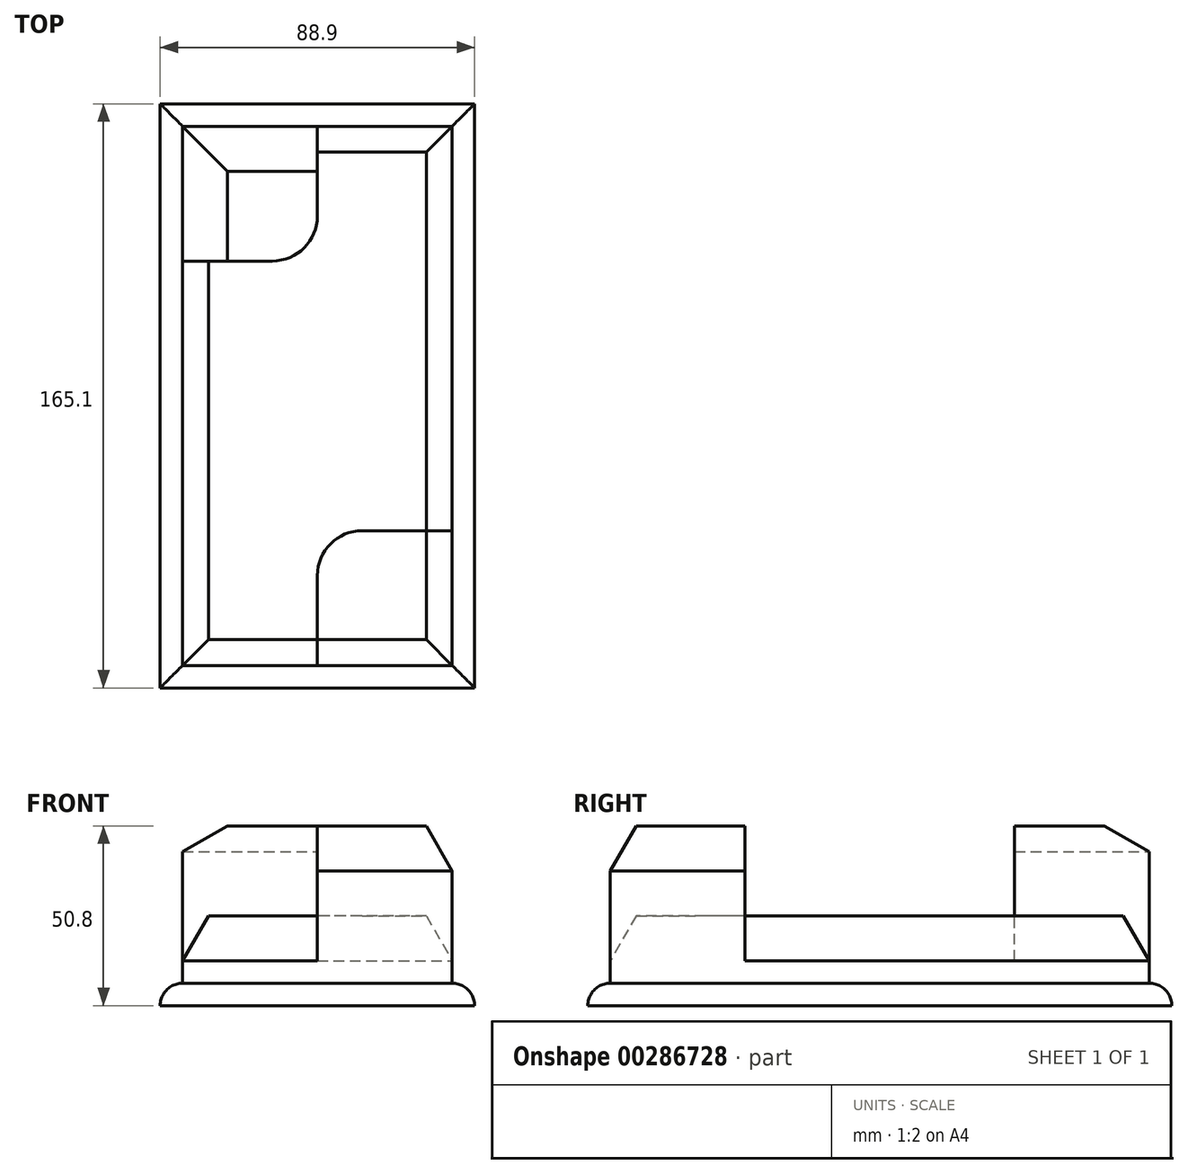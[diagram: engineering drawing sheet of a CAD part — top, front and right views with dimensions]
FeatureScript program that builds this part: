
annotation { "Feature Type Name" : "Feature", "Feature Type Description" : "" }
export const myFeature = defineFeature(function(context is Context, id is Id, definition is map)
    precondition{}
    {
        {
            var Q0;
            Q0=qCreatedBy(makeId("Top.planeOp"),FACE);
            var sketch = newSketch(context, id + "F0", { "sketchPlane" : qUnion([Q0])});
            skLineSegment(sketch, "E0.bottom", {"start": v(0, 0) * mm, "end": v(76.2, 0) * mm});
            skLineSegment(sketch, "E0.top", {"start": v(0, -152.4) * mm, "end": v(76.2, -152.4) * mm});
            skLineSegment(sketch, "E0.left", {"start": v(0, 0) * mm, "end": v(0, -152.4) * mm});
            skLineSegment(sketch, "E0.right", {"start": v(76.2, 0) * mm, "end": v(76.2, -152.4) * mm});
            skLineSegment(sketch, "E1.0", {"start": v(-6.35, 6.35) * mm, "end": v(82.55, 6.35) * mm});
            skLineSegment(sketch, "E1.1", {"start": v(-6.35, 6.35) * mm, "end": v(-6.35, -158.75) * mm});
            skLineSegment(sketch, "E1.2", {"start": v(-6.35, -158.75) * mm, "end": v(82.55, -158.75) * mm});
            skLineSegment(sketch, "E1.3", {"start": v(82.55, 6.35) * mm, "end": v(82.55, -158.75) * mm});
            skPoint(sketch, "E2", {"position": v(38.1, 0) * mm});
            skLineSegment(sketch, "E3", {"start": v(38.1, 0) * mm, "end": v(38.1, -25.4) * mm});
            skLineSegment(sketch, "E4", {"start": v(25.4, -38.1) * mm, "end": v(0, -38.1) * mm});
            skPoint(sketch, "E5.visualSharp", {"position": v(38.1, -38.1) * mm});
            skArc(sketch, "E5.filletArc", {"start": v(25.4, -38.1) * mm, "mid": v(34.38, -34.38) * mm, "end": v(38.1, -25.4) * mm});
            skLineSegment(sketch, "E6", {"start": v(38.1, -152.4) * mm, "end": v(38.1, -127) * mm});
            skLineSegment(sketch, "E7", {"start": v(50.8, -114.3) * mm, "end": v(76.2, -114.3) * mm});
            skPoint(sketch, "E8.visualSharp", {"position": v(38.1, -114.3) * mm});
            skArc(sketch, "E8.filletArc", {"start": v(50.8, -114.3) * mm, "mid": v(41.82, -118.02) * mm, "end": v(38.1, -127) * mm});
            skSolve(sketch);
        }
        {
            var Q0;
            Q0=makeQuery(id+"F0.imprint","IMPRINT",FACE,{"disambiguationData":[TD([[makeQuery(id+"F0.imprint","IMPRINT",EDGE,{"derivedFrom":sQuery(id+"F0.wireOp",EDGE,"E1.0")}),-1.0]])]});
            extrude(context, id + "F1", {"entities" : qUnion([Q0]), "depth" : 6.35 * mm});
        }
        {
            var Q0;
            {var subQ9=sQuery(id+"F0.wireOp",EDGE,"E3");Q0=makeQuery(id+"F0.imprint","IMPRINT",FACE,{"disambiguationData":[TD([[makeQuery(id+"F0.imprint","IMPRINT",EDGE,{"derivedFrom":subQ9}),1.0]])]});}
            extrude(context, id + "F2", {"entities" : qUnion([Q0]), "operationType" : NewBodyOperationType.ADD, "depth" : 25.4 * mm});
        }
        {
            var Q0;
            {var subQ1=sQuery(id+"F0.wireOp",EDGE,"E3");Q0=makeQuery(id+"F0.imprint","IMPRINT",FACE,{"disambiguationData":[TD([[makeQuery(id+"F0.imprint","IMPRINT",EDGE,{"derivedFrom":subQ1}),-1.0]])]});}
            var Q1;
            {var subQ1=sQuery(id+"F0.wireOp",EDGE,"E6");Q1=makeQuery(id+"F0.imprint","IMPRINT",FACE,{"disambiguationData":[TD([[makeQuery(id+"F0.imprint","IMPRINT",EDGE,{"derivedFrom":subQ1}),-1.0]])]});}
            extrude(context, id + "F3", {"entities" : qUnion([Q0, Q1]), "operationType" : NewBodyOperationType.ADD, "depth" : 50.8 * mm});
        }
        {
            var Q0;
            Q0=makeQuery(id+"F1.opExtrude","CAP_EDGE",EDGE,{"disambiguationData":[OSD([sQuery(id+"F0.wireOp",EDGE,"E1.2")])],"isStart":false});
            var Q1;
            Q1=makeQuery(id+"F1.opExtrude","CAP_EDGE",EDGE,{"disambiguationData":[OSD([sQuery(id+"F0.wireOp",EDGE,"E1.3")])],"isStart":false});
            var Q2;
            Q2=makeQuery(id+"F1.opExtrude","CAP_EDGE",EDGE,{"disambiguationData":[OSD([sQuery(id+"F0.wireOp",EDGE,"E1.1")])],"isStart":false});
            var Q3;
            Q3=makeQuery(id+"F1.opExtrude","CAP_EDGE",EDGE,{"disambiguationData":[OSD([sQuery(id+"F0.wireOp",EDGE,"E1.0")])],"isStart":false});
            fillet(context, id + "F4", {"entities" : qUnion([Q0, Q1, Q2, Q3]), "radius" : 6.35 * mm, "tangentPropagation" : true, "allowEdgeOverflow" : false});
        }
        {
            var Q0;
            Q0=makeQuery(id+"F2.opExtrude","CAP_EDGE",EDGE,{"disambiguationData":[OSD([sQuery(id+"F0.wireOp",EDGE,"E0.left")])],"isStart":false});
            var Q1;
            Q1=makeQuery(id+"F2.opExtrude","CAP_EDGE",EDGE,{"disambiguationData":[OSD([sQuery(id+"F0.wireOp",EDGE,"E0.top")])],"isStart":false});
            var Q2;
            Q2=makeQuery(id+"F2.opExtrude","CAP_EDGE",EDGE,{"disambiguationData":[OSD([sQuery(id+"F0.wireOp",EDGE,"E0.right")])],"isStart":false});
            var Q3;
            Q3=makeQuery(id+"F2.opExtrude","CAP_EDGE",EDGE,{"disambiguationData":[OSD([sQuery(id+"F0.wireOp",EDGE,"E0.bottom")])],"isStart":false});
            var Q4;
            Q4=makeQuery(id+"F3.opExtrude","CAP_EDGE",EDGE,{"disambiguationData":[OSD([sQuery(id+"F0.wireOp",EDGE,"E0.top")])],"isStart":false});
            var Q5;
            Q5=makeQuery(id+"F3.opExtrude","CAP_EDGE",EDGE,{"disambiguationData":[OSD([sQuery(id+"F0.wireOp",EDGE,"E0.bottom")])],"isStart":false});
            chamfer(context, id + "F5", {"entities" : qUnion([Q0, Q1, Q2, Q3, Q4, Q5]), "chamferType" : ChamferType.OFFSET_ANGLE, "width" : 12.7 * mm, "oppositeDirection" : true, "angle" : 30 * degree, "tangentPropagation" : true});
        }
        {
            var Q0;
            Q0=makeQuery(id+"F3.opExtrude","CAP_EDGE",EDGE,{"disambiguationData":[OSD([sQuery(id+"F0.wireOp",EDGE,"E0.left")])],"isStart":false});
            var Q1;
            Q1=makeQuery(id+"F3.opExtrude","CAP_EDGE",EDGE,{"disambiguationData":[OSD([sQuery(id+"F0.wireOp",EDGE,"E0.right")])],"isStart":false});
            chamfer(context, id + "F6", {"entities" : qUnion([Q0, Q1]), "chamferType" : ChamferType.OFFSET_ANGLE, "width" : 12.7 * mm, "oppositeDirection" : false, "angle" : 30 * degree, "tangentPropagation" : true});
        }
    });
